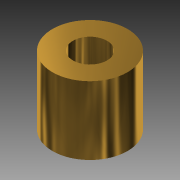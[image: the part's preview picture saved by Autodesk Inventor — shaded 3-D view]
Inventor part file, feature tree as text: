
AUTODESK INVENTOR PART (.ipt)
format: ipt  version: 2013 (Build 170138000, 138)  size: 96,768 bytes
history: native  units: mm
features: extrude x1, sketch x1
ambient origin geometry x8: Origin, YZ Plane, XZ Plane, XY Plane, X Axis, Y Axis, Z Axis, Center Point
bodies: Solid1 (feature_tree)
feature tree (2):
  extrude  "Extrusion1"  Depth=22.0mm
  sketch  "Sketch1"  dims[d0=10.0mm d2=22.0mm d3=20.0mm d4=0.0mm]
